# Revit family: QF_BOURGEAT_Self_Meuble_caisse_rampe_gauche
name_source: partatom
category: Equipement spécialisé
revit_build: Autodesk Revit 2015 (Build: 20140606_1530(x64)
units: mm (PartAtom-declared; Revit-internal decimal feet)

## types (2) — shared parameters
Certification = NF alimentaire
Charge max = 150.00 kg
Fabricant = BOURGEAT
Hauteur hors tout = 900 mm
Longueur hors tout = 1534 mm  [stored 5.03281 ft]
Nature isolant = Laine de verre
Poids net à vide = 115.00 kg
Profondeur hors tout = 820 mm
Spécification du Fabricant = Meuble_de caisse rampe à gauche OASIS
URL catalogue = http://www.bourgeat.fr
lgconsole = 1490 mm  [stored 4.88845 ft]
lgmeuble = 1466 mm  [stored 4.80971 ft]

## per-type parameters (varying)
| type | Modèle | Pieds | Roues |
| meuble_avec_pieds | 854510 | Oui | Non |
| meuble_avec_roues | 854510+854950 | Non | Oui |

note: [stored X ft] marks values corroborated as IEEE doubles in the binary element streams (Revit-internal decimal feet)

## geometry (parser evidence)
native form markers: Blend x12
no freeform markers — native parametric forms only
